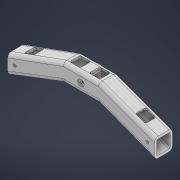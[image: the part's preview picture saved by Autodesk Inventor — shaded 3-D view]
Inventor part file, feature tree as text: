
AUTODESK INVENTOR PART (.ipt)
format: ipt  version: 2021 (Build 250183000, 183)  size: 545,280 bytes
history: native  units: mm
features: extrude x10, sketch x10, fillet x2, shell x1
ambient origin geometry x8: Origin, YZ Plane, XZ Plane, XY Plane, X Axis, Y Axis, Z Axis, Center Point
bodies: Volumenkörper1 (feature_tree)
feature tree (23):
  extrude  "Extrusion1"  Depth=66.0mm
  fillet  "Rundung3"  Radius=66.0mm
  shell  "Wandung3"  Thickness=3.490659mm
  extrude  "Extrusion8"  Depth=20.0mm
  extrude  "Extrusion9"  Depth=12.0mm
  extrude  "Extrusion10"  Depth=15.0mm
  fillet  "Rundung7"  Radius=3.0mm
  extrude  "Extrusion14"  Depth=12.0mm
  extrude  "Extrusion17"  Depth=3.0mm TaperAngle=0.0deg
  extrude  "Extrusion18"  Depth=12.0mm
  extrude  "Extrusion19"  Depth=12.0mm
  extrude  "Extrusion20"  Depth=3.0mm
  extrude  "Extrusion21"  Depth=8.5mm
  sketch  "Skizze1"  dims[d0=40.0mm d3=66.0mm d7=66.0mm d8=3.490659mm]
  sketch  "Skizze6"  dims[d9=20.0mm d10=0.0mm d19=4.0mm]
  sketch  "Skizze7"  dims[d48=2.6mm d51=12.0mm]
  sketch  "Skizze8"  dims[d52=12.0mm d53=15.0mm d55=3.0mm d56=0.0mm]
  sketch  "Skizze12"  dims[d57=12.0mm d58=12.0mm]
  sketch  "Skizze13"  dims[d59=15.0mm d61=3.0mm d62=0.0mm]
  sketch  "Skizze14"  dims[d63=12.0mm d64=12.0mm]
  sketch  "Skizze15"  dims[d66=3.0mm d67=12.0mm]
  sketch  "Skizze16"  dims[d68=12.0mm d70=3.0mm]
  sketch  "Skizze17"  dims[d71=3.0mm d72=0.0mm d73=2.0mm d87=10.0mm d89=3.490659mm d92=10.0mm d95=40.0mm d98=4.0mm d99=4.0mm d106=21.216mm d107=21.216mm d108=3.2mm d109=8.0mm d110=24.0mm d111=3.490659mm d112=3.2mm d113=8.0mm d114=27.925268mm d115=5.0mm d116=0.0mm d117=4.0mm d118=4.0mm d119=9.0mm d120=9.0mm d125=12.0mm d126=12.0mm d127=10.0mm d128=0.0mm d129=10.0mm d130=0.0mm d131=7.0mm d132=1.0mm d133=0.0mm d134=3.2mm d135=1.0mm d136=0.0mm d137=17.0mm d138=8.5mm d139=8.5mm d140=1.0mm d141=0.0mm]
